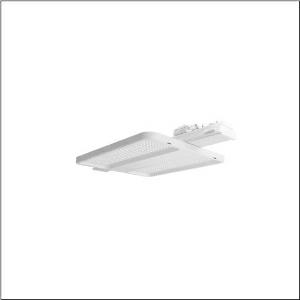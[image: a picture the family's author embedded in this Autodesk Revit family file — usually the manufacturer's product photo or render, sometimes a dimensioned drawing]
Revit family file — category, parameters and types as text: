
# Revit family: highbay_11_fur_licross_r__tragschiene_midi_51hn12da4fla02_4749
name_source: partatom
category: Lighting Fixtures
units: mm (PartAtom-declared; Revit-internal decimal feet)

## family parameters
Cut with Voids When Loaded = No
Host = Face
Light Source = No
Part Type = Normal
Room Calculation Point = No
Round Connector Dimension = Use Diameter
Shared = No

## types (1)
- --- (1 x LED, 15000 lm, 73.7 W, 4000K)
    Apparent Load = 74 VA
    CIE Flux Codes = 87 98 100 100 100
    Color Rendering = 80
    Color Temperature = 4000K
    Default Elevation = 1800 mm
    Description = high bay luminaire Highbay 11 for Licross® trunking rail midi; direct symmetric wide distribution, light control with lens of PMMA; UGR ≤ 22 (X = 4H | Y = 8H | S = 0.25H | reflection values 70/50/20); luminous flux: 15.000lm; light colour: 840, colour temperature: 4000K, MacAdam ≤ 2 SDCM (initial), colour rendering: CRI > 80; luminous efficacy: 203,5lm/W; rated service life: 100.000h (L95/B50) at AT= 25°C; control: Bluetooth® Mesh; for wireless networking: Node luminaire for setting up a local control solution without a higher-level application controller, intelligence completely in the luminaire; no control line such as DALI between the Node multi-sensor luminaires and Nodes is required, wireless integration of other Node luminaires and Node multi-sensor luminaires into the network is possible; number of Node luminaires in the project can be expanded as required, network sizes > 300 Nodes can be realized; can also be connected to lighting or building automation via various gateways upon request; integrated DALI2 ECG provides luminaire data (according to IEC62386, Part 251), energy data (Part 252), and monitoring and analytics data (Part 253) to higher-level systems for further processing; luminaire connection: plug, 5-pole, with phase selectionmains connection: 230..240V, AC 50/60Hz; connected load: 73,7W; protection rating (complete): IP64; insulation class (complete): insulation class I (protective earthing); protection symbol: D; impact resistance: IK07; certification: CE, ENEC, VDE, UKCA; internal wiring halogen-free; luminaire corresponds to IFS (International Featured Standards) requirements for safety and quality in the food industry; LABS conformity tested according to VDMA 24364:2018-05; housing frame of high-performance plastic PA6, matt traffic white (RAL 9016); cover of PMMA; fixing on rail side of steel, galvanised, white; blank cover of PC/ABS, traffic white (RAL 9016); dimension (LxWxH): 750 x 442 x 72mm; permissible operating ambient temperature: -20..+40°C (reducing of maximum allowable ambient temperature of 5°C with ceiling mounting); packaging unit: 1 piece
    Height = 72 mm  [stored 0.23622 ft]
    Lamp = 1 x LED
    Lamp Light Flux = 15000 lm
    Lamp Power = 73.7 W
    Lamp count = 1
    Length = 474 mm
    Luminous efficacy = 204 lm/W
    Manufacturer = Siteco
    ModVariant = No
    Model = 51HN12DA4FLA02
    Mounting Place = Ceiling
    Mounting Type = Pendant
    Number of Poles = 1
    OnlyDefault = Yes
    Power Factor = 1
    Product Name = Highbay 11 für Licross® Tragschiene midi
    Product group = high bay luminaire
    ProductGroupID = 901
    Protection Class = Protection class I
    Protection Degree = IP 64
    RLX_Detail_Level = 1
    RLX_Emergency_Light_Flux = 0 lm
    RLX_Emergency_Type = 0
    RLX_Emergency_Type_DB = No
    RlxData = <blob elided: 17941 chars, md5=3f4395f4>
    Socket = socket
    Standby Power = 0 W
    System Light Flux = 15000 lm
    System Power = 74 W
    Type Comments = factory setting: luminous flux: 100 % | dim-lin: 254 | 339 mA
    Type Image = l_1363258.jpg
    URL = http://relux.com
    VarID = @adj_024649
    Voltage = 0 V
    Weight = 0.00 kg
    Width = 442 mm

note: [stored X ft] marks values corroborated as IEEE doubles in the binary element streams (Revit-internal decimal feet)

## geometry (parser evidence)
native form markers: Blend x4, Sweep x13
no freeform markers — native parametric forms only
